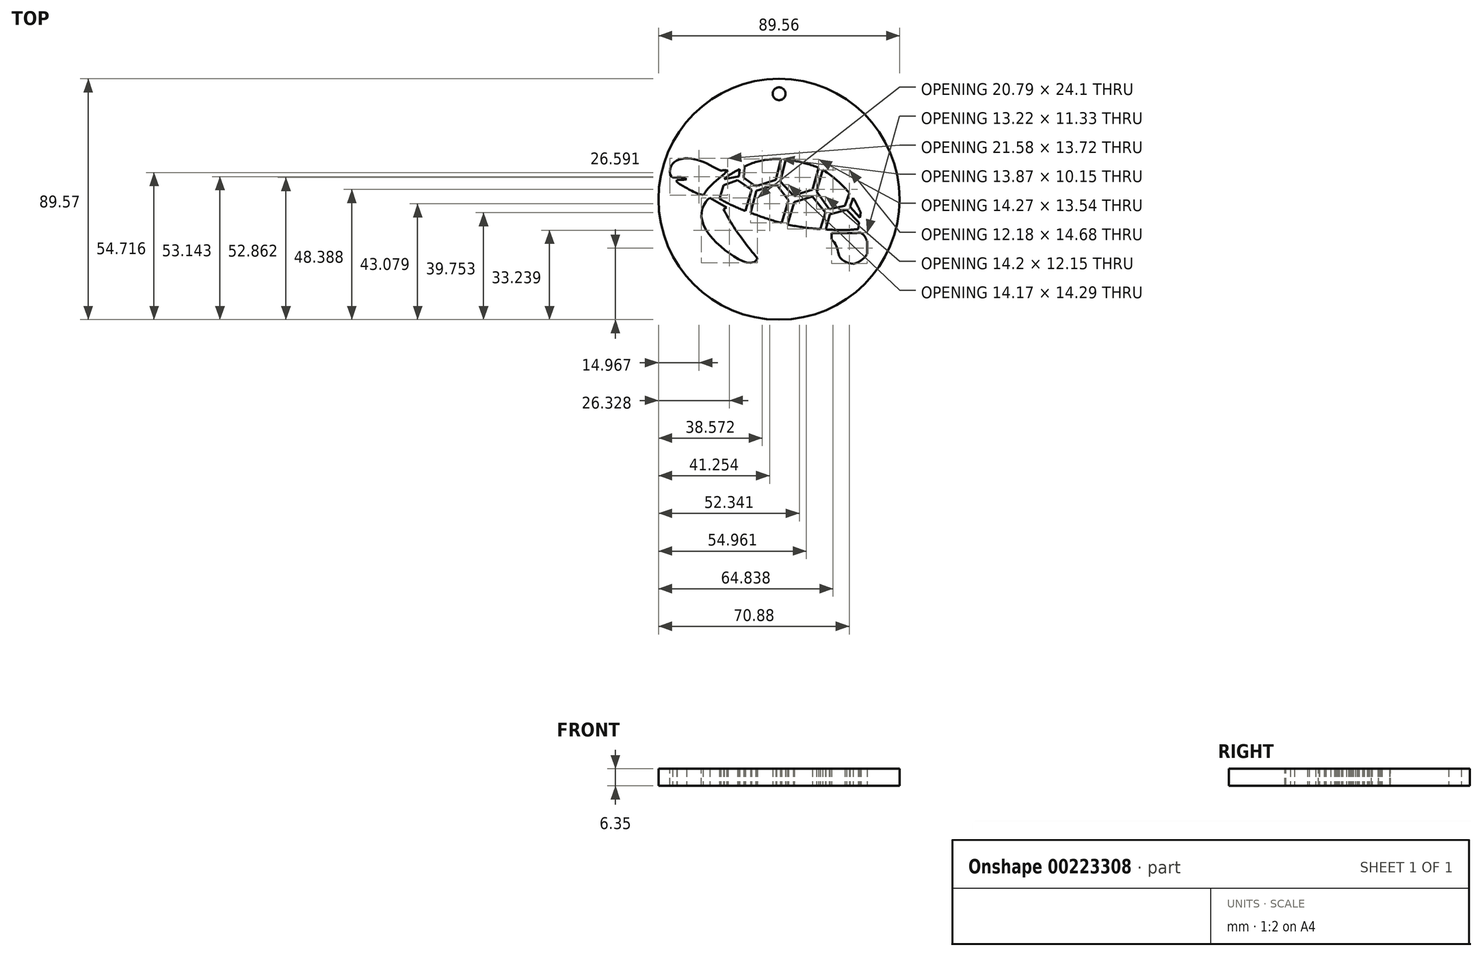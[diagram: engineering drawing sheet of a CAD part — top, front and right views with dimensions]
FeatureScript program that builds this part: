
annotation { "Feature Type Name" : "Feature", "Feature Type Description" : "" }
export const myFeature = defineFeature(function(context is Context, id is Id, definition is map)
    precondition{}
    {
        {
            var Q0;
            Q0=qCreatedBy(makeId("Top.planeOp"),FACE);
            var sketch = newSketch(context, id + "F0", { "sketchPlane" : qUnion([Q0])});
            skLineSegment(sketch, "E0", {"start": v(-26.03, 15.88) * mm, "end": v(-26.33, 11.75) * mm});
            skLineSegment(sketch, "E1", {"start": v(-26.33, 11.75) * mm, "end": v(-21.9, 8.59) * mm});
            skLineSegment(sketch, "E2", {"start": v(-21.9, 8.59) * mm, "end": v(-14.36, 10.96) * mm});
            skLineSegment(sketch, "E3", {"start": v(-14.36, 10.96) * mm, "end": v(-12.46, 18.73) * mm});
            skLineSegment(sketch, "E4", {"start": v(-10.68, 18.58) * mm, "end": v(-12.76, 10.33) * mm});
            skLineSegment(sketch, "E5", {"start": v(-12.76, 10.33) * mm, "end": v(-7.92, 5.04) * mm});
            skLineSegment(sketch, "E6", {"start": v(-7.92, 5.04) * mm, "end": v(-0.8, 7.28) * mm});
            skLineSegment(sketch, "E7", {"start": v(-0.8, 7.28) * mm, "end": v(1.5, 15.4) * mm});
            skLineSegment(sketch, "E8", {"start": v(2.98, 14.68) * mm, "end": v(0.78, 6.6) * mm});
            skLineSegment(sketch, "E9", {"start": v(0.78, 6.6) * mm, "end": v(5.48, 0) * mm});
            skLineSegment(sketch, "E10", {"start": v(5.48, 0) * mm, "end": v(11.28, 1.24) * mm});
            skLineSegment(sketch, "E11", {"start": v(11.28, 1.24) * mm, "end": v(12.96, 5.99) * mm});
            skLineSegment(sketch, "E12", {"start": v(14.3, 4.18) * mm, "end": v(13.17, 0.95) * mm});
            skLineSegment(sketch, "E13", {"start": v(13.17, 0.95) * mm, "end": v(16.88, -3.2) * mm});
            skLineSegment(sketch, "E14", {"start": v(16.88, -3.2) * mm, "end": v(17.08, -1.23) * mm});
            skLineSegment(sketch, "E15", {"start": v(4.13, -7.51) * mm, "end": v(5.75, -1.88) * mm});
            skLineSegment(sketch, "E16", {"start": v(5.75, -1.88) * mm, "end": v(11.96, -0.2) * mm});
            skLineSegment(sketch, "E17", {"start": v(11.96, -0.2) * mm, "end": v(16.52, -4.95) * mm});
            skLineSegment(sketch, "E18", {"start": v(16.52, -4.95) * mm, "end": v(16.24, -7.4) * mm});
            skLineSegment(sketch, "E19", {"start": v(2.11, -7.37) * mm, "end": v(4.09, -1.3) * mm});
            skLineSegment(sketch, "E20", {"start": v(4.09, -1.3) * mm, "end": v(-0.73, 4.78) * mm});
            skLineSegment(sketch, "E21", {"start": v(-0.73, 4.78) * mm, "end": v(-7.47, 2.69) * mm});
            skLineSegment(sketch, "E22", {"start": v(-7.47, 2.69) * mm, "end": v(-10.1, -5.63) * mm});
            skLineSegment(sketch, "E23", {"start": v(-12.24, -5.12) * mm, "end": v(-9.63, 3.36) * mm});
            skLineSegment(sketch, "E24", {"start": v(-9.63, 3.36) * mm, "end": v(-14.1, 9.17) * mm});
            skLineSegment(sketch, "E25", {"start": v(-14.1, 9.17) * mm, "end": v(-21.6, 6.94) * mm});
            skLineSegment(sketch, "E26", {"start": v(-21.6, 6.94) * mm, "end": v(-23.8, -1.33) * mm});
            skLineSegment(sketch, "E27", {"start": v(-25.73, -0.61) * mm, "end": v(-23.42, 7.24) * mm});
            skLineSegment(sketch, "E28", {"start": v(-23.42, 7.24) * mm, "end": v(-28.55, 10.8) * mm});
            skLineSegment(sketch, "E29", {"start": v(-28.55, 10.8) * mm, "end": v(-33.84, 8.96) * mm});
            skLineSegment(sketch, "E30", {"start": v(-33.84, 8.96) * mm, "end": v(-35.3, 3.89) * mm});
            skLineSegment(sketch, "E31", {"start": v(-33.6, 11.15) * mm, "end": v(-28.03, 12.2) * mm});
            skLineSegment(sketch, "E32", {"start": v(-28.03, 12.2) * mm, "end": v(-27.88, 14.92) * mm});
            skFitSpline(sketch, "E33", {"points": [v(-35.3, 3.89) * mm, v(-31.2, 1.72) * mm, v(-27.3, 0) * mm, v(-20.68, -2.45) * mm, v(-12.24, -5.12) * mm, v(-3.85, -6.79) * mm, v(1.83, -7.35) * mm, v(11.37, -7.75) * mm, v(16.24, -7.4) * mm], "startDerivative": vector(37.9, -22.3) * mm, "endDerivative": vector(32.15, 2.7) * mm});
            skFitSpline(sketch, "E34", {"points": [v(17.08, -1.23) * mm, v(15.96, 1.3) * mm, v(13.83, 4.86) * mm, v(11.24, 7.87) * mm, v(7.73, 11.25) * mm, v(2.55, 14.9) * mm, v(-3.3, 17.03) * mm, v(-8.34, 18.21) * mm, v(-13.18, 18.75) * mm, v(-18.68, 18.27) * mm, v(-23.78, 16.89) * mm, v(-28.86, 14.39) * mm, v(-31.6, 12.74) * mm, v(-33.6, 11.15) * mm], "startDerivative": vector(-16.03, 41.29) * mm, "endDerivative": vector(-32.46, -27.28) * mm});
            skFitSpline(sketch, "E35.trimOffspring", {"points": [v(17.08, -1.23) * mm, v(15.96, 1.3) * mm, v(13.83, 4.86) * mm, v(11.24, 7.87) * mm, v(7.73, 11.25) * mm, v(2.55, 14.9) * mm, v(-3.3, 17.03) * mm, v(-8.34, 18.21) * mm, v(-13.18, 18.75) * mm, v(-18.68, 18.27) * mm, v(-23.78, 16.89) * mm, v(-28.86, 14.39) * mm, v(-31.6, 12.74) * mm, v(-33.6, 11.15) * mm], "startDerivative": vector(-16.03, 41.29) * mm, "endDerivative": vector(-32.46, -27.28) * mm});
            skFitSpline(sketch, "E36.trimOffspring", {"points": [v(17.08, -1.23) * mm, v(15.96, 1.3) * mm, v(13.83, 4.86) * mm, v(11.24, 7.87) * mm, v(7.73, 11.25) * mm, v(2.55, 14.9) * mm, v(-3.3, 17.03) * mm, v(-8.34, 18.21) * mm, v(-13.18, 18.75) * mm, v(-18.68, 18.27) * mm, v(-23.78, 16.89) * mm, v(-28.86, 14.39) * mm, v(-31.6, 12.74) * mm, v(-33.6, 11.15) * mm], "startDerivative": vector(-16.03, 41.29) * mm, "endDerivative": vector(-32.46, -27.28) * mm});
            skLineSegment(sketch, "E37", {"start": v(-38.91, 4.24) * mm, "end": v(-32.66, 0.69) * mm});
            skLineSegment(sketch, "E38", {"start": v(-32.66, 0.69) * mm, "end": v(-33.8, 0) * mm});
            skFitSpline(sketch, "E39", {"points": [v(-33.8, 0) * mm, v(-31.23, -4.68) * mm, v(-27.73, -9.93) * mm, v(-23.67, -15.22) * mm, v(-21.25, -18.2) * mm], "startDerivative": vector(10.03, -18.59) * mm, "endDerivative": vector(10.16, -12.23) * mm});
            skFitSpline(sketch, "E40", {"points": [v(-38.91, 4.24) * mm, v(-40.06, 3.26) * mm, v(-41.16, 1.5) * mm, v(-42.02, -1.49) * mm, v(-41.49, -5.1) * mm, v(-39.33, -9.12) * mm, v(-35.32, -13.4) * mm, v(-30.7, -17.05) * mm, v(-26.62, -19.34) * mm, v(-23.93, -19.87) * mm, v(-21.74, -19.2) * mm, v(-21.25, -18.2) * mm], "startDerivative": vector(-19.13, -14.23) * mm, "endDerivative": vector(5.1, 20.33) * mm});
            skFitSpline(sketch, "E41", {"points": [v(6.3, -8.83) * mm, v(11.12, -8.83) * mm, v(17.2, -8.8) * mm], "startDerivative": vector(9.94, -0.01) * mm, "endDerivative": vector(11.82, 0.07) * mm});
            skFitSpline(sketch, "E42", {"points": [v(17.2, -8.8) * mm, v(18.64, -10.14) * mm, v(19.52, -11.8) * mm], "startDerivative": vector(2.89, -1.97) * mm, "endDerivative": vector(2.2, -4.16) * mm});
            skLineSegment(sketch, "E43", {"start": v(19.52, -11.8) * mm, "end": v(19.52, -16.63) * mm});
            skLineSegment(sketch, "E44", {"start": v(6.3, -8.83) * mm, "end": v(6.3, -11.2) * mm});
            skFitSpline(sketch, "E45", {"points": [v(6.3, -11.2) * mm, v(7.43, -12.5) * mm, v(8.27, -14.28) * mm, v(8.8, -16.1) * mm, v(9.3, -17.66) * mm, v(11, -19.26) * mm, v(13.44, -20.2) * mm, v(15.89, -19.92) * mm, v(18.23, -18.26) * mm, v(19.52, -16.63) * mm], "startDerivative": vector(12.16, -12.09) * mm, "endDerivative": vector(11.57, 18.15) * mm});
            skFitSpline(sketch, "E46", {"points": [v(-41.36, 5.23) * mm, v(-39.31, 7.96) * mm, v(-35.97, 11.1) * mm, v(-32.21, 14.34) * mm], "startDerivative": vector(6.27, 9.17) * mm, "endDerivative": vector(10.49, 9.02) * mm});
            skFitSpline(sketch, "E47", {"points": [v(-32.21, 14.34) * mm, v(-33.47, 14.53) * mm, v(-34.78, 14.34) * mm], "startDerivative": vector(-2.52, 0.58) * mm, "endDerivative": vector(-2.6, -0.57) * mm});
            skFitSpline(sketch, "E48", {"points": [v(-34.78, 14.34) * mm, v(-37.28, 15.6) * mm, v(-40.75, 17.33) * mm, v(-44.18, 18.5) * mm, v(-47.54, 18.95) * mm, v(-50.62, 18.36) * mm, v(-52.34, 17.35) * mm, v(-53.57, 15.4) * mm, v(-53.54, 12.44) * mm, v(-52.68, 11.9) * mm], "startDerivative": vector(-21.25, 10.4) * mm, "endDerivative": vector(14.15, -4.93) * mm});
            skFitSpline(sketch, "E49", {"points": [v(-52.68, 11.9) * mm, v(-51.2, 11.9) * mm, v(-49.5, 11.9) * mm, v(-47.54, 11.18) * mm], "startDerivative": vector(4.4, -0.11) * mm, "endDerivative": vector(4.92, -2.3) * mm});
            skFitSpline(sketch, "E50", {"points": [v(-47.54, 11.18) * mm, v(-48.82, 10.97) * mm, v(-51.13, 10.9) * mm], "startDerivative": vector(-2.77, -0.55) * mm, "endDerivative": vector(-4.33, 0) * mm});
            skFitSpline(sketch, "E51", {"points": [v(-41.36, 5.23) * mm, v(-43.11, 5.75) * mm, v(-46.3, 7.17) * mm, v(-48.51, 8.46) * mm, v(-50.27, 9.52) * mm, v(-51.12, 10.22) * mm, v(-51.13, 10.9) * mm], "startDerivative": vector(-9.61, 2.42) * mm, "endDerivative": vector(1.32, 7.13) * mm});
            skSolve(sketch);
        }
        {
            var Q0;
            Q0=qCreatedBy(makeId("Top.planeOp"),FACE);
            var sketch = newSketch(context, id + "F1", { "sketchPlane" : qUnion([Q0])});
            skCircle(sketch, "E52", {"center": v(-13.19, 3.73) * mm, "radius": 44.78 * mm});
            skCircle(sketch, "E53", {"center": v(-13.19, 42.94) * mm, "radius": 2.38 * mm});
            skSolve(sketch);
        }
        {
            var Q0;
            Q0=makeQuery(id+"F1.imprint","IMPRINT",FACE,{"disambiguationData":[TD([[makeQuery(id+"F1.imprint","IMPRINT",EDGE,{"derivedFrom":sQuery(id+"F1.wireOp",EDGE,"E52")}),1.0]])]});
            extrude(context, id + "F2", {"entities" : qUnion([Q0]), "depth" : 6.35 * mm});
        }
        {
            var Q0;
            Q0 = qSketchRegion(id + "F0", true);
            extrude(context, id + "F3", {"entities" : qUnion([Q0]), "operationType" : NewBodyOperationType.REMOVE, "depth" : 6.35 * mm});
        }
    });
